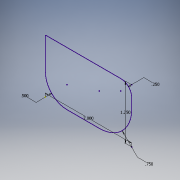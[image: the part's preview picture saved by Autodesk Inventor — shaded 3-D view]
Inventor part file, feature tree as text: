
AUTODESK INVENTOR PART (.ipt)
format: ipt  version: 2017 (Build 210142000, 142)  size: 90,112 bytes
history: native  units: in
note: dims shown in document units (in); Inventor stores cm internally (conversion verified against a paired STEP export)
features: sketch x1
ambient origin geometry x8: Origin, YZ Plane, XZ Plane, XY Plane, X Axis, Y Axis, Z Axis, Center Point
feature tree (1):
  sketch  "Sketch1"  dims[d0=2.0in d1=1.25in d2=0.25in d3=0.75in d4=0.5in]
